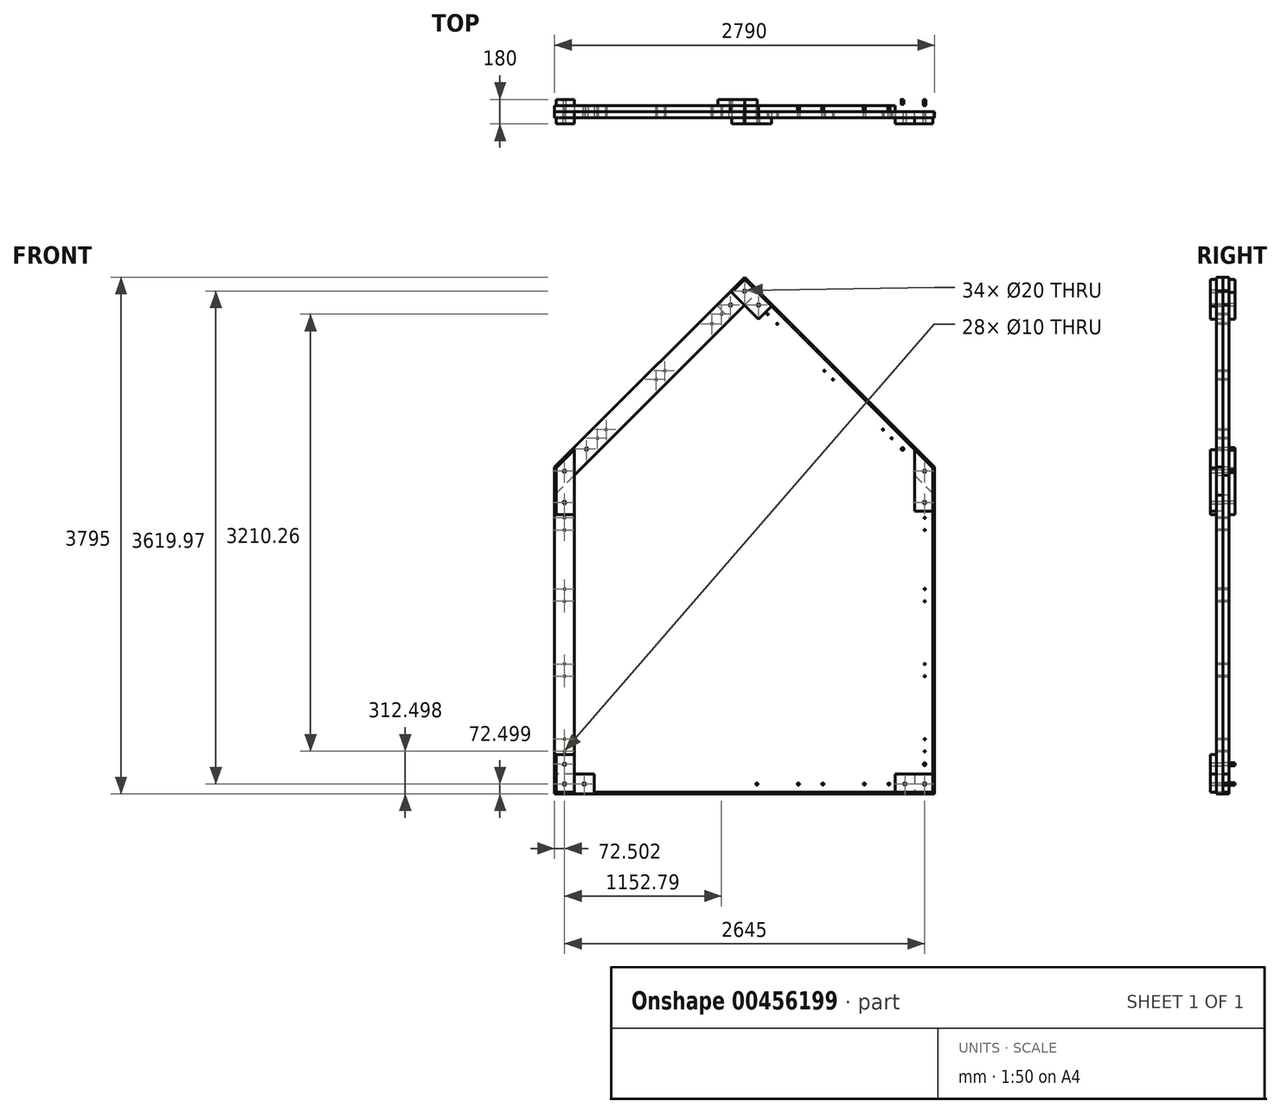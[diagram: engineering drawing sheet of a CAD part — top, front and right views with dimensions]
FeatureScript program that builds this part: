
annotation { "Feature Type Name" : "Feature", "Feature Type Description" : "" }
export const myFeature = defineFeature(function(context is Context, id is Id, definition is map)
    precondition{}
    {
        {
            var Q0;
            Q0=qCreatedBy(makeId("Front.planeOp"),FACE);
            var sketch = newSketch(context, id + "F0", { "sketchPlane" : qUnion([Q0])});
            skLineSegment(sketch, "E0.bottom", {"start": v(-2120.6, 125.67) * mm, "end": v(-4620.6, 125.67) * mm});
            skLineSegment(sketch, "E0.top", {"start": v(-2120.6, -2069.27) * mm, "end": v(-4620.6, -2069.27) * mm});
            skLineSegment(sketch, "E0.left", {"start": v(-2120.6, 125.67) * mm, "end": v(-2120.6, -2069.27) * mm});
            skLineSegment(sketch, "E0.right", {"start": v(-4620.6, 125.67) * mm, "end": v(-4620.6, -2069.27) * mm});
            skLineSegment(sketch, "E1", {"start": v(-4620.6, 125.67) * mm, "end": v(-3370.6, 1375.67) * mm});
            skPoint(sketch, "E1.endSnap0", {"position": v(-3370.6, 125.67) * mm});
            skLineSegment(sketch, "E2", {"start": v(-3370.6, 1375.67) * mm, "end": v(-2120.6, 125.67) * mm});
            skLineSegment(sketch, "E3.0", {"start": v(-3370.6, 1580.73) * mm, "end": v(-1975.6, 185.73) * mm});
            skLineSegment(sketch, "E3.1", {"start": v(-4765.6, 185.73) * mm, "end": v(-3370.6, 1580.73) * mm});
            skLineSegment(sketch, "E3.2", {"start": v(-1975.6, 185.73) * mm, "end": v(-1975.6, -2214.27) * mm});
            skLineSegment(sketch, "E3.3", {"start": v(-1975.6, -2214.27) * mm, "end": v(-4765.6, -2214.27) * mm});
            skLineSegment(sketch, "E3.4", {"start": v(-4765.6, 185.73) * mm, "end": v(-4765.6, -2214.27) * mm});
            skLineSegment(sketch, "E4", {"start": v(-4620.6, -2069.27) * mm, "end": v(-4765.6, -2069.27) * mm});
            skLineSegment(sketch, "E5", {"start": v(-4620.6, -2069.27) * mm, "end": v(-4620.6, -2214.27) * mm});
            skLineSegment(sketch, "E6", {"start": v(-2120.6, -2069.27) * mm, "end": v(-1975.6, -2069.27) * mm});
            skLineSegment(sketch, "E7", {"start": v(-2120.6, -2069.27) * mm, "end": v(-2120.6, -2214.27) * mm});
            skLineSegment(sketch, "E8", {"start": v(-3370.6, 1375.67) * mm, "end": v(-3268.07, 1478.2) * mm});
            skLineSegment(sketch, "E9", {"start": v(-3370.6, 1375.67) * mm, "end": v(-3473.13, 1478.2) * mm});
            skLineSegment(sketch, "E10", {"start": v(-4620.6, 125.67) * mm, "end": v(-4620.6, 330.73) * mm});
            skLineSegment(sketch, "E11", {"start": v(-4620.6, 125.67) * mm, "end": v(-4765.6, -19.33) * mm});
            skLineSegment(sketch, "E12", {"start": v(-2120.6, 125.67) * mm, "end": v(-1975.6, -19.33) * mm});
            skLineSegment(sketch, "E13", {"start": v(-2120.6, 125.67) * mm, "end": v(-2120.6, 330.73) * mm});
            skLineSegment(sketch, "E14", {"start": v(-4620.6, 125.67) * mm, "end": v(-4765.6, 185.73) * mm, "construction": true});
            skLineSegment(sketch, "E15", {"start": v(-4765.6, -1924.27) * mm, "end": v(-4620.6, -1924.27) * mm});
            skPoint(sketch, "E16", {"position": v(-4693.1, 155.7) * mm});
            skLineSegment(sketch, "E17", {"start": v(-4765.6, -134.3) * mm, "end": v(-4620.6, -134.3) * mm});
            skLineSegment(sketch, "E18", {"start": v(-4539.3, 412.02) * mm, "end": v(-4436.77, 309.5) * mm});
            skPoint(sketch, "E19", {"position": v(-4693.1, -74.3) * mm});
            skLineSegment(sketch, "E20", {"start": v(-3575.66, 1375.67) * mm, "end": v(-3473.13, 1273.14) * mm});
            skLineSegment(sketch, "E21", {"start": v(-4475.6, -2069.27) * mm, "end": v(-4475.6, -2214.27) * mm});
            skLineSegment(sketch, "E22", {"start": v(-4488.04, 360.76) * mm, "end": v(-3524.4, 1324.4) * mm, "construction": true});
            skPoint(sketch, "E23", {"position": v(-4440.3, 408.49) * mm});
            skPoint(sketch, "E24", {"position": v(-3572.12, 1276.67) * mm});
            skPoint(sketch, "E25", {"position": v(-4006.22, 842.58) * mm});
            skLineSegment(sketch, "E26", {"start": v(-2265.6, -2069.27) * mm, "end": v(-2265.6, -2214.27) * mm});
            skLineSegment(sketch, "E27", {"start": v(-4475.6, -2141.77) * mm, "end": v(-2265.6, -2141.77) * mm, "construction": true});
            skPoint(sketch, "E28", {"position": v(-4340.6, -2141.77) * mm});
            skPoint(sketch, "E29", {"position": v(-2400.6, -2141.77) * mm});
            skPoint(sketch, "E30", {"position": v(-3370.6, -2141.77) * mm});
            skLineSegment(sketch, "E31", {"start": v(-4340.6, -2141.77) * mm, "end": v(-3370.6, -2141.77) * mm, "construction": true});
            skLineSegment(sketch, "E32", {"start": v(-3370.6, -2141.77) * mm, "end": v(-2400.6, -2141.77) * mm, "construction": true});
            skPoint(sketch, "E33", {"position": v(-3855.6, -2141.77) * mm});
            skPoint(sketch, "E34", {"position": v(-2885.6, -2141.77) * mm});
            skLineSegment(sketch, "E35", {"start": v(-4693.1, 155.7) * mm, "end": v(-4488.04, 360.76) * mm, "construction": true});
            skPoint(sketch, "E36", {"position": v(-4693.1, -1996.77) * mm});
            skPoint(sketch, "E36.positionSnap0", {"position": v(-4693.1, -2069.27) * mm});
            skPoint(sketch, "E37", {"position": v(-4693.1, -2141.77) * mm});
            skPoint(sketch, "E38", {"position": v(-4548.1, -2141.77) * mm});
            skPoint(sketch, "E39.positionSnap0", {"position": v(-4693.1, -1924.27) * mm});
            skPoint(sketch, "E40", {"position": v(-4693.1, -174.3) * mm});
            skPoint(sketch, "E41.MirrorP", {"position": v(-4459.75, 389.04) * mm});
            skCircle(sketch, "E42", {"center": v(-4693.1, -1996.77) * mm, "radius": 10 * mm});
            skCircle(sketch, "E43", {"center": v(-4693.1, -2141.77) * mm, "radius": 10 * mm});
            skCircle(sketch, "E44", {"center": v(-4548.1, -2141.77) * mm, "radius": 10 * mm});
            skLineSegment(sketch, "E45", {"start": v(-3524.4, 1324.4) * mm, "end": v(-3421.86, 1426.93) * mm, "construction": true});
            skLineSegment(sketch, "E46", {"start": v(-3421.86, 1426.93) * mm, "end": v(-3319.33, 1529.46) * mm, "construction": true});
            skPoint(sketch, "E47", {"position": v(-3473.13, 1375.67) * mm});
            skPoint(sketch, "E48", {"position": v(-3370.6, 1478.2) * mm});
            skCircle(sketch, "E49", {"center": v(-3473.13, 1375.67) * mm, "radius": 10 * mm});
            skCircle(sketch, "E50", {"center": v(-3370.6, 1478.2) * mm, "radius": 10 * mm});
            skLineSegment(sketch, "E51", {"start": v(-3370.6, -2069.27) * mm, "end": v(-3370.6, -1584.54) * mm, "construction": true});
            skCircle(sketch, "E52.MirrorC", {"center": v(-2193.1, -2141.77) * mm, "radius": 10 * mm});
            skCircle(sketch, "E53.MirrorC", {"center": v(-2048.1, -2141.77) * mm, "radius": 10 * mm});
            skLineSegment(sketch, "E54.MirrorCS", {"start": v(-1975.6, -1924.27) * mm, "end": v(-2120.6, -1924.27) * mm});
            skCircle(sketch, "E55.MirrorC", {"center": v(-2048.1, -1996.77) * mm, "radius": 10 * mm});
            skCircle(sketch, "E56", {"center": v(-4693.1, 155.7) * mm, "radius": 10 * mm});
            skCircle(sketch, "E57", {"center": v(-4693.1, -74.3) * mm, "radius": 10 * mm});
            skCircle(sketch, "E58", {"center": v(-4530.46, 318.33) * mm, "radius": 10 * mm});
            skCircle(sketch, "E59.MirrorC", {"center": v(-2048.1, -74.3) * mm, "radius": 10 * mm});
            skCircle(sketch, "E60.MirrorC", {"center": v(-2048.1, 155.7) * mm, "radius": 10 * mm});
            skCircle(sketch, "E61.MirrorC", {"center": v(-2210.73, 318.33) * mm, "radius": 10 * mm});
            skCircle(sketch, "E62.MirrorC", {"center": v(-3268.07, 1375.67) * mm, "radius": 10 * mm});
            skLineSegment(sketch, "E63", {"start": v(-4620.6, -2024.27) * mm, "end": v(-2120.6, -2024.27) * mm});
            skLineSegment(sketch, "E64.0", {"start": v(-3370.6, 1340.31) * mm, "end": v(-2138.28, 107.99) * mm});
            skLineSegment(sketch, "E64.1", {"start": v(-4602.92, 107.99) * mm, "end": v(-3370.6, 1340.31) * mm});
            skLineSegment(sketch, "E65", {"start": v(-4595.6, -2024.27) * mm, "end": v(-4595.6, 115.31) * mm});
            skLineSegment(sketch, "E66", {"start": v(-4595.6, 115.31) * mm, "end": v(-4620.6, 125.67) * mm});
            skLineSegment(sketch, "E67.MirrorCS", {"start": v(-2145.6, -2024.27) * mm, "end": v(-2145.6, 115.31) * mm});
            skLineSegment(sketch, "E68", {"start": v(-3370.6, 1375.67) * mm, "end": v(-3370.6, 1340.31) * mm});
            skLineSegment(sketch, "E69", {"start": v(-2145.6, 115.31) * mm, "end": v(-2120.6, 125.67) * mm});
            skSolve(sketch);
        }
        {
            var Q0;
            {var subQ1=sQuery(id+"F0.wireOp",EDGE,"E4");Q0=makeQuery(id+"F0.imprint","IMPRINT",FACE,{"disambiguationData":[TD([[makeQuery(id+"F0.imprint","IMPRINT",EDGE,{"derivedFrom":subQ1}),1.0]])]});}
            var Q1;
            {var subQ0=sQuery(id+"F0.wireOp",EDGE,"E15");Q1=makeQuery(id+"F0.imprint","IMPRINT",FACE,{"disambiguationData":[TD([[makeQuery(id+"F0.imprint","IMPRINT",EDGE,{"derivedFrom":subQ0}),1.0]])]});}
            var Q2;
            {var subQ1=sQuery(id+"F0.wireOp",EDGE,"E4");Q2=makeQuery(id+"F0.imprint","IMPRINT",FACE,{"disambiguationData":[TD([[makeQuery(id+"F0.imprint","IMPRINT",EDGE,{"derivedFrom":subQ1}),-1.0]])]});}
            var Q3;
            {var subQ0=sQuery(id+"F0.wireOp",EDGE,"E11");Q3=makeQuery(id+"F0.imprint","IMPRINT",FACE,{"disambiguationData":[TD([[makeQuery(id+"F0.imprint","IMPRINT",EDGE,{"derivedFrom":subQ0}),1.0]])]});}
            extrude(context, id + "F1", {"entities" : qUnion([Q0, Q1, Q2, Q3]), "depth" : -45 * mm, "offsetDistance" : 25 * mm});
        }
        {
            var Q0;
            {var subQ1=sQuery(id+"F0.wireOp",EDGE,"E9");Q0=makeQuery(id+"F0.imprint","IMPRINT",FACE,{"disambiguationData":[TD([[makeQuery(id+"F0.imprint","IMPRINT",EDGE,{"derivedFrom":subQ1}),1.0]])]});}
            var Q1;
            {var subQ0=sQuery(id+"F0.wireOp",EDGE,"E18");Q1=makeQuery(id+"F0.imprint","IMPRINT",FACE,{"disambiguationData":[TD([[makeQuery(id+"F0.imprint","IMPRINT",EDGE,{"derivedFrom":subQ0}),1.0]])]});}
            var Q2;
            {var subQ0=sQuery(id+"F0.wireOp",EDGE,"E10");Q2=makeQuery(id+"F0.imprint","IMPRINT",FACE,{"disambiguationData":[TD([[makeQuery(id+"F0.imprint","IMPRINT",EDGE,{"derivedFrom":subQ0}),-1.0]])]});}
            var Q3;
            {var subQ4=sQuery(id+"F0.wireOp",EDGE,"E10");Q3=makeQuery(id+"F0.imprint","IMPRINT",FACE,{"disambiguationData":[TD([[makeQuery(id+"F0.imprint","IMPRINT",EDGE,{"derivedFrom":subQ4}),1.0]])]});}
            extrude(context, id + "F2", {"entities" : qUnion([Q0, Q1, Q2, Q3]), "depth" : -45 * mm, "offsetDistance" : 25 * mm});
        }
        {
            var Q0;
            {var subQ0=sQuery(id+"F0.wireOp",EDGE,"E8");Q0=makeQuery(id+"F0.imprint","IMPRINT",FACE,{"disambiguationData":[TD([[makeQuery(id+"F0.imprint","IMPRINT",EDGE,{"derivedFrom":subQ0}),1.0]])]});}
            var Q1;
            Q1=makeQuery(id+"F0.imprint","IMPRINT",FACE,{"disambiguationData":[TD([[makeQuery(id+"F0.imprint","IMPRINT",EDGE,{"derivedFrom":sQuery(id+"F0.wireOp",EDGE,"E2")}),1.0]])]});
            extrude(context, id + "F3", {"entities" : qUnion([Q0, Q1]), "depth" : -45 * mm, "offsetDistance" : 25 * mm});
        }
        {
            var Q0;
            {var subQ1=sQuery(id+"F0.wireOp",EDGE,"E12");Q0=makeQuery(id+"F0.imprint","IMPRINT",FACE,{"disambiguationData":[TD([[makeQuery(id+"F0.imprint","IMPRINT",EDGE,{"derivedFrom":subQ1}),1.0]])]});}
            var Q1;
            {var subQ1=sQuery(id+"F0.wireOp",EDGE,"E12");Q1=makeQuery(id+"F0.imprint","IMPRINT",FACE,{"disambiguationData":[TD([[makeQuery(id+"F0.imprint","IMPRINT",EDGE,{"derivedFrom":subQ1}),-1.0]])]});}
            var Q2;
            {var subQ0=sQuery(id+"F0.wireOp",EDGE,"E6");Q2=makeQuery(id+"F0.imprint","IMPRINT",FACE,{"disambiguationData":[TD([[makeQuery(id+"F0.imprint","IMPRINT",EDGE,{"derivedFrom":subQ0}),1.0]])]});}
            extrude(context, id + "F4", {"entities" : qUnion([Q0, Q1, Q2]), "depth" : -45 * mm, "offsetDistance" : 25 * mm});
        }
        {
            var Q0;
            {var subQ0=sQuery(id+"F0.wireOp",EDGE,"E21");Q0=makeQuery(id+"F0.imprint","IMPRINT",FACE,{"disambiguationData":[TD([[makeQuery(id+"F0.imprint","IMPRINT",EDGE,{"derivedFrom":subQ0}),1.0]])]});}
            var Q1;
            {var subQ1=sQuery(id+"F0.wireOp",EDGE,"E5");Q1=makeQuery(id+"F0.imprint","IMPRINT",FACE,{"disambiguationData":[TD([[makeQuery(id+"F0.imprint","IMPRINT",EDGE,{"derivedFrom":subQ1}),1.0]])]});}
            var Q2;
            {var subQ1=sQuery(id+"F0.wireOp",EDGE,"E7");Q2=makeQuery(id+"F0.imprint","IMPRINT",FACE,{"disambiguationData":[TD([[makeQuery(id+"F0.imprint","IMPRINT",EDGE,{"derivedFrom":subQ1}),-1.0]])]});}
            var Q3;
            {var subQ1=sQuery(id+"F0.wireOp",EDGE,"E6");Q3=makeQuery(id+"F0.imprint","IMPRINT",FACE,{"disambiguationData":[TD([[makeQuery(id+"F0.imprint","IMPRINT",EDGE,{"derivedFrom":subQ1}),-1.0]])]});}
            extrude(context, id + "F5", {"entities" : qUnion([Q0, Q1, Q2, Q3]), "depth" : -45 * mm, "offsetDistance" : 25 * mm});
        }
        {
            var Q0;
            {var subQ1=sQuery(id+"F0.wireOp",EDGE,"E4");Q0=makeQuery(id+"F0.imprint","IMPRINT",FACE,{"disambiguationData":[TD([[makeQuery(id+"F0.imprint","IMPRINT",EDGE,{"derivedFrom":subQ1}),1.0]])]});}
            var Q1;
            {var subQ1=sQuery(id+"F0.wireOp",EDGE,"E5");Q1=makeQuery(id+"F0.imprint","IMPRINT",FACE,{"disambiguationData":[TD([[makeQuery(id+"F0.imprint","IMPRINT",EDGE,{"derivedFrom":subQ1}),1.0]])]});}
            var Q2;
            {var subQ0=sQuery(id+"F0.wireOp",EDGE,"E21");Q2=makeQuery(id+"F0.imprint","IMPRINT",FACE,{"disambiguationData":[TD([[makeQuery(id+"F0.imprint","IMPRINT",EDGE,{"derivedFrom":subQ0}),1.0]])]});}
            var Q3;
            {var subQ1=sQuery(id+"F0.wireOp",EDGE,"E7");Q3=makeQuery(id+"F0.imprint","IMPRINT",FACE,{"disambiguationData":[TD([[makeQuery(id+"F0.imprint","IMPRINT",EDGE,{"derivedFrom":subQ1}),-1.0]])]});}
            extrude(context, id + "F6", {"entities" : qUnion([Q0, Q1, Q2, Q3]), "depth" : 45 * mm, "offsetDistance" : 25 * mm});
        }
        {
            var Q0;
            {var subQ1=sQuery(id+"F0.wireOp",EDGE,"E4");Q0=makeQuery(id+"F0.imprint","IMPRINT",FACE,{"disambiguationData":[TD([[makeQuery(id+"F0.imprint","IMPRINT",EDGE,{"derivedFrom":subQ1}),-1.0]])]});}
            var Q1;
            {var subQ0=sQuery(id+"F0.wireOp",EDGE,"E15");Q1=makeQuery(id+"F0.imprint","IMPRINT",FACE,{"disambiguationData":[TD([[makeQuery(id+"F0.imprint","IMPRINT",EDGE,{"derivedFrom":subQ0}),1.0]])]});}
            var Q2;
            {var subQ0=sQuery(id+"F0.wireOp",EDGE,"E11");Q2=makeQuery(id+"F0.imprint","IMPRINT",FACE,{"disambiguationData":[TD([[makeQuery(id+"F0.imprint","IMPRINT",EDGE,{"derivedFrom":subQ0}),1.0]])]});}
            var Q3;
            {var subQ4=sQuery(id+"F0.wireOp",EDGE,"E10");Q3=makeQuery(id+"F0.imprint","IMPRINT",FACE,{"disambiguationData":[TD([[makeQuery(id+"F0.imprint","IMPRINT",EDGE,{"derivedFrom":subQ4}),1.0]])]});}
            extrude(context, id + "F7", {"entities" : qUnion([Q0, Q1, Q2, Q3]), "depth" : 45 * mm, "offsetDistance" : 25 * mm});
        }
        {
            var Q0;
            {var subQ0=sQuery(id+"F0.wireOp",EDGE,"E10");Q0=makeQuery(id+"F0.imprint","IMPRINT",FACE,{"disambiguationData":[TD([[makeQuery(id+"F0.imprint","IMPRINT",EDGE,{"derivedFrom":subQ0}),-1.0]])]});}
            var Q1;
            {var subQ0=sQuery(id+"F0.wireOp",EDGE,"E18");Q1=makeQuery(id+"F0.imprint","IMPRINT",FACE,{"disambiguationData":[TD([[makeQuery(id+"F0.imprint","IMPRINT",EDGE,{"derivedFrom":subQ0}),1.0]])]});}
            var Q2;
            {var subQ1=sQuery(id+"F0.wireOp",EDGE,"E9");Q2=makeQuery(id+"F0.imprint","IMPRINT",FACE,{"disambiguationData":[TD([[makeQuery(id+"F0.imprint","IMPRINT",EDGE,{"derivedFrom":subQ1}),1.0]])]});}
            var Q3;
            {var subQ0=sQuery(id+"F0.wireOp",EDGE,"E8");Q3=makeQuery(id+"F0.imprint","IMPRINT",FACE,{"disambiguationData":[TD([[makeQuery(id+"F0.imprint","IMPRINT",EDGE,{"derivedFrom":subQ0}),1.0]])]});}
            extrude(context, id + "F8", {"entities" : qUnion([Q0, Q1, Q2, Q3]), "depth" : 45 * mm, "offsetDistance" : 25 * mm});
        }
        {
            var Q0;
            Q0=makeQuery(id+"F0.imprint","IMPRINT",FACE,{"disambiguationData":[TD([[makeQuery(id+"F0.imprint","IMPRINT",EDGE,{"derivedFrom":sQuery(id+"F0.wireOp",EDGE,"E2")}),1.0]])]});
            var Q1;
            {var subQ1=sQuery(id+"F0.wireOp",EDGE,"E12");Q1=makeQuery(id+"F0.imprint","IMPRINT",FACE,{"disambiguationData":[TD([[makeQuery(id+"F0.imprint","IMPRINT",EDGE,{"derivedFrom":subQ1}),1.0]])]});}
            extrude(context, id + "F9", {"entities" : qUnion([Q0, Q1]), "depth" : 45 * mm, "offsetDistance" : 25 * mm});
        }
        {
            var Q0;
            {var subQ1=sQuery(id+"F0.wireOp",EDGE,"E12");Q0=makeQuery(id+"F0.imprint","IMPRINT",FACE,{"disambiguationData":[TD([[makeQuery(id+"F0.imprint","IMPRINT",EDGE,{"derivedFrom":subQ1}),-1.0]])]});}
            var Q1;
            {var subQ0=sQuery(id+"F0.wireOp",EDGE,"E6");Q1=makeQuery(id+"F0.imprint","IMPRINT",FACE,{"disambiguationData":[TD([[makeQuery(id+"F0.imprint","IMPRINT",EDGE,{"derivedFrom":subQ0}),1.0]])]});}
            var Q2;
            {var subQ1=sQuery(id+"F0.wireOp",EDGE,"E6");Q2=makeQuery(id+"F0.imprint","IMPRINT",FACE,{"disambiguationData":[TD([[makeQuery(id+"F0.imprint","IMPRINT",EDGE,{"derivedFrom":subQ1}),-1.0]])]});}
            extrude(context, id + "F10", {"entities" : qUnion([Q0, Q1, Q2]), "depth" : 45 * mm, "offsetDistance" : 25 * mm});
        }
        {
            var Q0;
            Q0=makeQuery(id+"F7.opExtrude","CAP_FACE",FACE,{"disambiguationData":[OSD([sQuery(id+"F0.wireOp",EDGE,"E0.right"),sQuery(id+"F0.wireOp",EDGE,"E3.1"),sQuery(id+"F0.wireOp",EDGE,"E3.4"),sQuery(id+"F0.wireOp",EDGE,"E4"),sQuery(id+"F0.wireOp",EDGE,"E10"),sQuery(id+"F0.wireOp",EDGE,"E42"),sQuery(id+"F0.wireOp",EDGE,"E56"),sQuery(id+"F0.wireOp",EDGE,"E57")])],"isStart":false});
            var sketch = newSketch(context, id + "F11", { "sketchPlane" : qUnion([Q0])});
            skLineSegment(sketch, "E70.bottom", {"start": v(-4765.6, -2069.27) * mm, "end": v(-1975.6, -2069.27) * mm});
            skLineSegment(sketch, "E70.top", {"start": v(-4765.6, -2214.27) * mm, "end": v(-1975.6, -2214.27) * mm});
            skLineSegment(sketch, "E70.left", {"start": v(-4765.6, -2069.27) * mm, "end": v(-4765.6, -2214.27) * mm});
            skLineSegment(sketch, "E70.right", {"start": v(-1975.6, -2069.27) * mm, "end": v(-1975.6, -2214.27) * mm});
            skLineSegment(sketch, "E71", {"start": v(-4765.6, -2069.27) * mm, "end": v(-4765.6, 185.73) * mm});
            skLineSegment(sketch, "E72", {"start": v(-1975.6, -2069.27) * mm, "end": v(-1975.6, 185.73) * mm});
            skLineSegment(sketch, "E73", {"start": v(-4765.6, 185.73) * mm, "end": v(-3370.6, 1580.73) * mm});
            skLineSegment(sketch, "E74", {"start": v(-3370.6, 1580.73) * mm, "end": v(-1975.6, 185.73) * mm});
            skLineSegment(sketch, "E75.0", {"start": v(-3370.6, 1375.67) * mm, "end": v(-2120.6, 125.67) * mm});
            skLineSegment(sketch, "E75.1", {"start": v(-4620.6, 125.67) * mm, "end": v(-3370.6, 1375.67) * mm});
            skLineSegment(sketch, "E75.2", {"start": v(-2120.6, -2069.27) * mm, "end": v(-2120.6, 125.67) * mm});
            skLineSegment(sketch, "E75.3", {"start": v(-4620.6, -2069.27) * mm, "end": v(-2120.6, -2069.27) * mm});
            skLineSegment(sketch, "E75.4", {"start": v(-4620.6, -2069.27) * mm, "end": v(-4620.6, 125.67) * mm});
            skLineSegment(sketch, "E76", {"start": v(-4620.6, 125.67) * mm, "end": v(-4765.6, -19.33) * mm});
            skLineSegment(sketch, "E77", {"start": v(-4765.6, -164.33) * mm, "end": v(-4620.6, -164.33) * mm});
            skLineSegment(sketch, "E78", {"start": v(-4518.07, 433.26) * mm, "end": v(-4415.54, 330.73) * mm});
            skCircle(sketch, "E79", {"center": v(-4693.1, -74.3) * mm, "radius": 10 * mm});
            skCircle(sketch, "E80", {"center": v(-4693.1, 155.7) * mm, "radius": 10 * mm});
            skCircle(sketch, "E81", {"center": v(-4693.1, -1996.77) * mm, "radius": 10 * mm});
            skLineSegment(sketch, "E82", {"start": v(-4693.1, 155.7) * mm, "end": v(-3319.33, 1529.46) * mm, "construction": true});
            skPoint(sketch, "E83", {"position": v(-3370.6, 1478.2) * mm});
            skPoint(sketch, "E84", {"position": v(-3473.13, 1375.67) * mm});
            skPoint(sketch, "E85", {"position": v(-4530.46, 318.33) * mm});
            skCircle(sketch, "E86", {"center": v(-4530.46, 318.33) * mm, "radius": 10 * mm});
            skCircle(sketch, "E87", {"center": v(-4693.1, -2141.77) * mm, "radius": 10 * mm});
            skCircle(sketch, "E88", {"center": v(-4548.1, -2141.77) * mm, "radius": 10 * mm});
            skLineSegment(sketch, "E89", {"start": v(-4475.6, -2069.27) * mm, "end": v(-4475.6, -2214.27) * mm});
            skLineSegment(sketch, "E90", {"start": v(-4765.6, -1924.27) * mm, "end": v(-4620.6, -1924.27) * mm});
            skLineSegment(sketch, "E91", {"start": v(-4620.6, -2069.27) * mm, "end": v(-4620.6, -2214.27) * mm});
            skLineSegment(sketch, "E92", {"start": v(-3370.6, 1375.67) * mm, "end": v(-3473.13, 1478.2) * mm});
            skLineSegment(sketch, "E93", {"start": v(-3268.07, 1273.14) * mm, "end": v(-3165.54, 1375.67) * mm});
            skLineSegment(sketch, "E94", {"start": v(-3370.6, 1478.2) * mm, "end": v(-3268.07, 1375.67) * mm, "construction": true});
            skCircle(sketch, "E95", {"center": v(-3370.6, 1478.2) * mm, "radius": 10 * mm});
            skCircle(sketch, "E96", {"center": v(-3268.07, 1375.67) * mm, "radius": 10 * mm});
            skLineSegment(sketch, "E97", {"start": v(-2120.6, 125.67) * mm, "end": v(-2120.6, 330.73) * mm});
            skLineSegment(sketch, "E98", {"start": v(-2120.6, -139.1) * mm, "end": v(-1975.6, -139.1) * mm});
            skLineSegment(sketch, "E99", {"start": v(-2048.1, -139.1) * mm, "end": v(-2048.1, 258.23) * mm, "construction": true});
            skLineSegment(sketch, "E100", {"start": v(-3268.07, 1375.67) * mm, "end": v(-1975.6, 83.2) * mm, "construction": true});
            skCircle(sketch, "E101", {"center": v(-2048.1, 155.7) * mm, "radius": 10 * mm});
            skCircle(sketch, "E102", {"center": v(-2048.1, -74.3) * mm, "radius": 10 * mm});
            skLineSegment(sketch, "E103", {"start": v(-2265.6, -2069.27) * mm, "end": v(-2265.6, -2214.27) * mm});
            skLineSegment(sketch, "E104", {"start": v(-2265.6, -2141.77) * mm, "end": v(-1975.6, -2141.77) * mm, "construction": true});
            skCircle(sketch, "E105", {"center": v(-2048.1, -2141.77) * mm, "radius": 10 * mm});
            skCircle(sketch, "E106", {"center": v(-2193.1, -2141.77) * mm, "radius": 10 * mm});
            skLineSegment(sketch, "E107.0", {"start": v(-4753.6, -2069.27) * mm, "end": v(-4753.6, -2202.27) * mm});
            skLineSegment(sketch, "E107.1", {"start": v(-4753.6, -2202.27) * mm, "end": v(-1987.6, -2202.27) * mm});
            skLineSegment(sketch, "E107.2", {"start": v(-4753.6, 180.76) * mm, "end": v(-3370.6, 1563.76) * mm});
            skLineSegment(sketch, "E107.3", {"start": v(-3370.6, 1563.76) * mm, "end": v(-1987.6, 180.76) * mm});
            skLineSegment(sketch, "E107.4", {"start": v(-1987.6, -2069.27) * mm, "end": v(-1987.6, 180.76) * mm});
            skLineSegment(sketch, "E107.5", {"start": v(-4753.6, -2069.27) * mm, "end": v(-4753.6, 180.76) * mm});
            skLineSegment(sketch, "E107.6", {"start": v(-1987.6, -2069.27) * mm, "end": v(-1987.6, -2202.27) * mm});
            skLineSegment(sketch, "E108", {"start": v(-4475.6, -2141.77) * mm, "end": v(-2265.6, -2141.77) * mm, "construction": true});
            skLineSegment(sketch, "E109", {"start": v(-4693.1, -164.33) * mm, "end": v(-4693.1, -1924.27) * mm, "construction": true});
            skCircle(sketch, "E110", {"center": v(-4430.6, -2141.77) * mm, "radius": 8 * mm});
            skCircle(sketch, "E111", {"center": v(-4250.6, -2141.77) * mm, "radius": 8 * mm});
            skCircle(sketch, "E112", {"center": v(-3945.6, -2141.77) * mm, "radius": 8 * mm});
            skCircle(sketch, "E113", {"center": v(-4693.1, -1901.77) * mm, "radius": 5 * mm});
            skCircle(sketch, "E114", {"center": v(-4693.1, -1811.77) * mm, "radius": 5 * mm});
            skCircle(sketch, "E115", {"center": v(-4693.1, -1350.77) * mm, "radius": 5 * mm});
            skCircle(sketch, "E116", {"center": v(-4693.1, -1260.77) * mm, "radius": 5 * mm});
            skCircle(sketch, "E117", {"center": v(-4693.1, -799.77) * mm, "radius": 5 * mm});
            skCircle(sketch, "E118", {"center": v(-4693.1, -709.77) * mm, "radius": 5 * mm});
            skCircle(sketch, "E119", {"center": v(-4693.1, -186.83) * mm, "radius": 5 * mm});
            skCircle(sketch, "E120", {"center": v(-4693.1, -276.83) * mm, "radius": 5 * mm});
            skCircle(sketch, "E121", {"center": v(-4450.9, 397.9) * mm, "radius": 5 * mm});
            skCircle(sketch, "E122", {"center": v(-4387.25, 461.54) * mm, "radius": 5 * mm});
            skCircle(sketch, "E123", {"center": v(-3540.3, 1308.5) * mm, "radius": 5 * mm});
            skCircle(sketch, "E124", {"center": v(-3611.01, 1237.78) * mm, "radius": 5 * mm});
            skCircle(sketch, "E125", {"center": v(-4019.56, 829.24) * mm, "radius": 5 * mm});
            skCircle(sketch, "E126", {"center": v(-3955.92, 892.88) * mm, "radius": 5 * mm});
            skCircle(sketch, "E127", {"center": v(-3765.6, -2141.77) * mm, "radius": 8 * mm});
            skCircle(sketch, "E128", {"center": v(-3460.6, -2141.77) * mm, "radius": 8 * mm});
            skLineSegment(sketch, "E129", {"start": v(-3370.6, -2202.27) * mm, "end": v(-3370.6, -2069.27) * mm, "construction": true});
            skCircle(sketch, "E130.MirrorC", {"center": v(-3200.9, 1308.5) * mm, "radius": 5 * mm});
            skCircle(sketch, "E131.MirrorC", {"center": v(-3130.18, 1237.78) * mm, "radius": 5 * mm});
            skCircle(sketch, "E132.MirrorC", {"center": v(-2721.64, 829.24) * mm, "radius": 5 * mm});
            skCircle(sketch, "E133.MirrorC", {"center": v(-2353.94, 461.54) * mm, "radius": 5 * mm});
            skCircle(sketch, "E134.MirrorC", {"center": v(-2290.3, 397.9) * mm, "radius": 5 * mm});
            skCircle(sketch, "E135.MirrorC", {"center": v(-2048.1, -186.83) * mm, "radius": 5 * mm});
            skCircle(sketch, "E136.MirrorC", {"center": v(-2048.1, -276.83) * mm, "radius": 5 * mm});
            skCircle(sketch, "E137.MirrorC", {"center": v(-2048.1, -709.77) * mm, "radius": 5 * mm});
            skCircle(sketch, "E138.MirrorC", {"center": v(-2048.1, -799.77) * mm, "radius": 5 * mm});
            skCircle(sketch, "E139.MirrorC", {"center": v(-2048.1, -1260.77) * mm, "radius": 5 * mm});
            skCircle(sketch, "E140.MirrorC", {"center": v(-2048.1, -1350.77) * mm, "radius": 5 * mm});
            skCircle(sketch, "E141.MirrorC", {"center": v(-2048.1, -1811.77) * mm, "radius": 5 * mm});
            skCircle(sketch, "E142.MirrorC", {"center": v(-2048.1, -1901.77) * mm, "radius": 5 * mm});
            skCircle(sketch, "E143.MirrorC", {"center": v(-2310.6, -2141.77) * mm, "radius": 8 * mm});
            skCircle(sketch, "E144.MirrorC", {"center": v(-2490.6, -2141.77) * mm, "radius": 8 * mm});
            skCircle(sketch, "E145.MirrorC", {"center": v(-2795.6, -2141.77) * mm, "radius": 8 * mm});
            skCircle(sketch, "E146.MirrorC", {"center": v(-2975.6, -2141.77) * mm, "radius": 8 * mm});
            skCircle(sketch, "E147.MirrorC", {"center": v(-3280.6, -2141.77) * mm, "radius": 8 * mm});
            skCircle(sketch, "E148.MirrorC", {"center": v(-2785.28, 892.88) * mm, "radius": 5 * mm});
            skSolve(sketch);
        }
        {
            var Q0;
            Q0=makeQuery(id+"F11.imprint","IMPRINT",FACE,{"disambiguationData":[TD([[makeQuery(id+"F11.imprint","IMPRINT",EDGE,{"derivedFrom":sQuery(id+"F11.wireOp",EDGE,"E79")}),-1.0]])]});
            var Q1;
            Q1=makeQuery(id+"F11.imprint","IMPRINT",FACE,{"disambiguationData":[TD([[makeQuery(id+"F11.imprint","IMPRINT",EDGE,{"derivedFrom":sQuery(id+"F11.wireOp",EDGE,"E80")}),-1.0]])]});
            var Q2;
            Q2=makeQuery(id+"F11.imprint","IMPRINT",FACE,{"disambiguationData":[TD([[makeQuery(id+"F11.imprint","IMPRINT",EDGE,{"derivedFrom":sQuery(id+"F11.wireOp",EDGE,"E81")}),-1.0]])]});
            var Q3;
            Q3=makeQuery(id+"F11.imprint","IMPRINT",FACE,{"disambiguationData":[TD([[makeQuery(id+"F11.imprint","IMPRINT",EDGE,{"derivedFrom":sQuery(id+"F11.wireOp",EDGE,"E87")}),-1.0]])]});
            var Q4;
            Q4=makeQuery(id+"F11.imprint","IMPRINT",FACE,{"disambiguationData":[TD([[makeQuery(id+"F11.imprint","IMPRINT",EDGE,{"derivedFrom":sQuery(id+"F11.wireOp",EDGE,"E105")}),-1.0]])]});
            var Q5;
            Q5=makeQuery(id+"F11.imprint","IMPRINT",FACE,{"disambiguationData":[TD([[makeQuery(id+"F11.imprint","IMPRINT",EDGE,{"derivedFrom":sQuery(id+"F11.wireOp",EDGE,"E101")}),-1.0]])]});
            var Q6;
            Q6=makeQuery(id+"F11.imprint","IMPRINT",FACE,{"disambiguationData":[TD([[makeQuery(id+"F11.imprint","IMPRINT",EDGE,{"derivedFrom":sQuery(id+"F11.wireOp",EDGE,"E95")}),-1.0]])]});
            extrude(context, id + "F12", {"entities" : qUnion([Q0, Q1, Q2, Q3, Q4, Q5, Q6]), "depth" : 45 * mm, "offsetDistance" : 25 * mm});
        }
        {
            var Q0;
            Q0=makeQuery(id+"F4.opExtrude","CAP_FACE",FACE,{"disambiguationData":[OSD([sQuery(id+"F0.wireOp",EDGE,"E0.left"),sQuery(id+"F0.wireOp",EDGE,"E3.0"),sQuery(id+"F0.wireOp",EDGE,"E3.2"),sQuery(id+"F0.wireOp",EDGE,"E6"),sQuery(id+"F0.wireOp",EDGE,"E13"),sQuery(id+"F0.wireOp",EDGE,"E55.MirrorC"),sQuery(id+"F0.wireOp",EDGE,"E59.MirrorC"),sQuery(id+"F0.wireOp",EDGE,"E60.MirrorC")])],"isStart":false});
            var sketch = newSketch(context, id + "F13", { "sketchPlane" : qUnion([Q0])});
            skLineSegment(sketch, "E149.bottom", {"start": v(1975.6, -2069.27) * mm, "end": v(4765.6, -2069.27) * mm});
            skLineSegment(sketch, "E149.top", {"start": v(1975.6, -2214.27) * mm, "end": v(4765.6, -2214.27) * mm});
            skLineSegment(sketch, "E149.left", {"start": v(1975.6, -2069.27) * mm, "end": v(1975.6, -2214.27) * mm});
            skLineSegment(sketch, "E149.right", {"start": v(4765.6, -2069.27) * mm, "end": v(4765.6, -2214.27) * mm});
            skLineSegment(sketch, "E150", {"start": v(1975.6, -2069.27) * mm, "end": v(1975.6, 185.73) * mm});
            skLineSegment(sketch, "E151", {"start": v(4765.6, -2069.27) * mm, "end": v(4765.6, 185.73) * mm});
            skLineSegment(sketch, "E152", {"start": v(1975.6, 185.73) * mm, "end": v(3370.6, 1580.73) * mm});
            skLineSegment(sketch, "E153", {"start": v(3370.6, 1580.73) * mm, "end": v(4765.6, 185.73) * mm});
            skLineSegment(sketch, "E154.0", {"start": v(4620.6, -2069.27) * mm, "end": v(4620.6, 125.67) * mm});
            skLineSegment(sketch, "E154.1", {"start": v(3370.6, 1375.67) * mm, "end": v(4620.6, 125.67) * mm});
            skLineSegment(sketch, "E154.2", {"start": v(2120.6, -2069.27) * mm, "end": v(4620.6, -2069.27) * mm});
            skLineSegment(sketch, "E154.3", {"start": v(2120.6, -2069.27) * mm, "end": v(2120.6, 125.67) * mm});
            skLineSegment(sketch, "E154.4", {"start": v(2120.6, 125.67) * mm, "end": v(3370.6, 1375.67) * mm});
            skLineSegment(sketch, "E155.bottom", {"start": v(1975.6, -2214.27) * mm, "end": v(2120.6, -2214.27) * mm});
            skLineSegment(sketch, "E155.top", {"start": v(1975.6, -1924.27) * mm, "end": v(2120.6, -1924.27) * mm});
            skLineSegment(sketch, "E155.left", {"start": v(1975.6, -2214.27) * mm, "end": v(1975.6, -1924.27) * mm});
            skLineSegment(sketch, "E155.right", {"start": v(2120.6, -2214.27) * mm, "end": v(2120.6, -1924.27) * mm});
            skLineSegment(sketch, "E156.bottom", {"start": v(4765.6, -2214.27) * mm, "end": v(4475.6, -2214.27) * mm});
            skLineSegment(sketch, "E156.top", {"start": v(4765.6, -2069.27) * mm, "end": v(4475.6, -2069.27) * mm});
            skLineSegment(sketch, "E156.left", {"start": v(4765.6, -2214.27) * mm, "end": v(4765.6, -2069.27) * mm});
            skLineSegment(sketch, "E156.right", {"start": v(4475.6, -2214.27) * mm, "end": v(4475.6, -2069.27) * mm});
            skLineSegment(sketch, "E157", {"start": v(3370.6, 1375.67) * mm, "end": v(3268.07, 1478.2) * mm});
            skLineSegment(sketch, "E158", {"start": v(3268.07, 1478.2) * mm, "end": v(3370.6, 1580.73) * mm});
            skLineSegment(sketch, "E159", {"start": v(3575.66, 1375.67) * mm, "end": v(3473.13, 1273.14) * mm});
            skLineSegment(sketch, "E160", {"start": v(3319.33, 1529.46) * mm, "end": v(4765.6, 83.2) * mm, "construction": true});
            skLineSegment(sketch, "E161", {"start": v(4765.6, -2214.27) * mm, "end": v(4620.6, -2214.27) * mm});
            skLineSegment(sketch, "E162", {"start": v(4693.1, -2214.27) * mm, "end": v(4693.1, 258.23) * mm, "construction": true});
            skLineSegment(sketch, "E163", {"start": v(2120.6, 125.67) * mm, "end": v(1975.6, -19.33) * mm});
            skLineSegment(sketch, "E164", {"start": v(2223.13, 433.26) * mm, "end": v(2325.66, 330.73) * mm});
            skLineSegment(sketch, "E165", {"start": v(4620.6, -164.33) * mm, "end": v(4765.6, -164.33) * mm});
            skLineSegment(sketch, "E166", {"start": v(4620.6, 125.67) * mm, "end": v(4620.6, 330.73) * mm});
            skLineSegment(sketch, "E167.0", {"start": v(4753.6, -2069.27) * mm, "end": v(4753.6, 180.76) * mm});
            skLineSegment(sketch, "E167.1", {"start": v(3370.6, 1563.76) * mm, "end": v(4753.6, 180.76) * mm});
            skLineSegment(sketch, "E167.2", {"start": v(1987.6, -2202.27) * mm, "end": v(4765.6, -2202.27) * mm});
            skLineSegment(sketch, "E167.3", {"start": v(1987.6, -2069.27) * mm, "end": v(1987.6, -2202.27) * mm});
            skLineSegment(sketch, "E167.4", {"start": v(1987.6, -2069.27) * mm, "end": v(1987.6, 180.76) * mm});
            skLineSegment(sketch, "E167.5", {"start": v(1987.6, 180.76) * mm, "end": v(3370.6, 1563.76) * mm});
            skSolve(sketch);
        }
        {
            var Q0;
            {var subQ3=sQuery(id+"F13.wireOp",EDGE,"E159");var subQ5=sQuery(id+"F13.wireOp",EDGE,"E154.1");var subQ6=makeQuery(id+"F13.imprint","INTERSECT",VERTEX,{"derivedFrom":[subQ5,subQ3]});Q0=makeQuery(id+"F13.imprint","IMPRINT",FACE,{"disambiguationData":[TD([[makeQuery(id+"F13.imprint","IMPRINT",EDGE,{"disambiguationData":[TD([[subQ6,1.0]])],"derivedFrom":subQ3}),-1.0]])]});}
            var Q1;
            Q1=makeQuery(id+"F13.imprint","IMPRINT",FACE,{"disambiguationData":[TD([[makeQuery(id+"F13.imprint","IMPRINT",EDGE,{"derivedFrom":makeQuery(id+"F4.opExtrude","CAP_EDGE",EDGE,{"disambiguationData":[OSD([sQuery(id+"F0.wireOp",EDGE,"E60.MirrorC")])],"isStart":false})}),-1.0]])]});
            var Q2;
            {var subQ0=sQuery(id+"F13.wireOp",EDGE,"E154.4");var subQ3=sQuery(id+"F13.wireOp",EDGE,"E164");var subQ4=makeQuery(id+"F13.imprint","INTERSECT",VERTEX,{"derivedFrom":[subQ0,subQ3]});Q2=makeQuery(id+"F13.imprint","IMPRINT",FACE,{"disambiguationData":[TD([[makeQuery(id+"F13.imprint","IMPRINT",EDGE,{"disambiguationData":[TD([[subQ4,1.0]])],"derivedFrom":subQ3}),-1.0]])]});}
            var Q3;
            Q3=makeQuery(id+"F13.imprint","IMPRINT",FACE,{"disambiguationData":[TD([[makeQuery(id+"F13.imprint","IMPRINT",EDGE,{"derivedFrom":makeQuery(id+"F4.opExtrude","CAP_EDGE",EDGE,{"disambiguationData":[OSD([sQuery(id+"F0.wireOp",EDGE,"E55.MirrorC")])],"isStart":false})}),-1.0]])]});
            var Q4;
            {var subQ3=sQuery(id+"F13.wireOp",EDGE,"E167.3");Q4=makeQuery(id+"F13.imprint","IMPRINT",FACE,{"disambiguationData":[TD([[makeQuery(id+"F13.imprint","IMPRINT",EDGE,{"derivedFrom":subQ3}),1.0]])]});}
            var Q5;
            {var subQ1=sQuery(id+"F13.wireOp",EDGE,"E156.top");var subQ5=makeQuery(id+"F13.imprint","INTERSECT",VERTEX,{"derivedFrom":[sQuery(id+"F13.wireOp",EDGE,"E154.0"),subQ1]});Q5=makeQuery(id+"F13.imprint","IMPRINT",FACE,{"disambiguationData":[TD([[makeQuery(id+"F13.imprint","IMPRINT",EDGE,{"disambiguationData":[TD([[subQ5,1.0]])],"derivedFrom":subQ1}),1.0]])]});}
            var Q6;
            {var subQ3=sQuery(id+"F13.wireOp",EDGE,"E165");var subQ5=sQuery(id+"F13.wireOp",EDGE,"E154.0");var subQ6=makeQuery(id+"F13.imprint","INTERSECT",VERTEX,{"derivedFrom":[subQ5,subQ3]});Q6=makeQuery(id+"F13.imprint","IMPRINT",FACE,{"disambiguationData":[TD([[makeQuery(id+"F13.imprint","IMPRINT",EDGE,{"disambiguationData":[TD([[subQ6,-1.0]])],"derivedFrom":subQ3}),1.0]])]});}
            extrude(context, id + "F14", {"entities" : qUnion([Q0, Q1, Q2, Q3, Q4, Q5, Q6]), "depth" : 45 * mm, "offsetDistance" : 25 * mm});
        }
        {
            var Q0;
            Q0=makeQuery(id+"F0.imprint","IMPRINT",FACE,{"disambiguationData":[TD([[makeQuery(id+"F0.imprint","IMPRINT",EDGE,{"derivedFrom":sQuery(id+"F0.wireOp",EDGE,"E49")}),1.0]])]});
            var Q1;
            Q1=makeQuery(id+"F0.imprint","IMPRINT",FACE,{"disambiguationData":[TD([[makeQuery(id+"F0.imprint","IMPRINT",EDGE,{"derivedFrom":sQuery(id+"F0.wireOp",EDGE,"E50")}),-1.0]])]});
            var Q2;
            Q2=makeQuery(id+"F0.imprint","IMPRINT",FACE,{"disambiguationData":[TD([[makeQuery(id+"F0.imprint","IMPRINT",EDGE,{"derivedFrom":sQuery(id+"F0.wireOp",EDGE,"E62.MirrorC")}),-1.0]])]});
            var Q3;
            Q3=makeQuery(id+"F0.imprint","IMPRINT",FACE,{"disambiguationData":[TD([[makeQuery(id+"F0.imprint","IMPRINT",EDGE,{"derivedFrom":sQuery(id+"F0.wireOp",EDGE,"E58")}),1.0]])]});
            var Q4;
            Q4=makeQuery(id+"F0.imprint","IMPRINT",FACE,{"disambiguationData":[TD([[makeQuery(id+"F0.imprint","IMPRINT",EDGE,{"derivedFrom":sQuery(id+"F0.wireOp",EDGE,"E56")}),1.0]])]});
            var Q5;
            Q5=makeQuery(id+"F0.imprint","IMPRINT",FACE,{"disambiguationData":[TD([[makeQuery(id+"F0.imprint","IMPRINT",EDGE,{"derivedFrom":sQuery(id+"F0.wireOp",EDGE,"E57")}),1.0]])]});
            var Q6;
            Q6=makeQuery(id+"F0.imprint","IMPRINT",FACE,{"disambiguationData":[TD([[makeQuery(id+"F0.imprint","IMPRINT",EDGE,{"derivedFrom":sQuery(id+"F0.wireOp",EDGE,"E42")}),1.0]])]});
            var Q7;
            Q7=makeQuery(id+"F0.imprint","IMPRINT",FACE,{"disambiguationData":[TD([[makeQuery(id+"F0.imprint","IMPRINT",EDGE,{"derivedFrom":sQuery(id+"F0.wireOp",EDGE,"E43")}),1.0]])]});
            var Q8;
            Q8=makeQuery(id+"F0.imprint","IMPRINT",FACE,{"disambiguationData":[TD([[makeQuery(id+"F0.imprint","IMPRINT",EDGE,{"derivedFrom":sQuery(id+"F0.wireOp",EDGE,"E44")}),1.0]])]});
            var Q9;
            Q9=makeQuery(id+"F0.imprint","IMPRINT",FACE,{"disambiguationData":[TD([[makeQuery(id+"F0.imprint","IMPRINT",EDGE,{"derivedFrom":sQuery(id+"F0.wireOp",EDGE,"E52.MirrorC")}),-1.0]])]});
            var Q10;
            Q10=makeQuery(id+"F0.imprint","IMPRINT",FACE,{"disambiguationData":[TD([[makeQuery(id+"F0.imprint","IMPRINT",EDGE,{"derivedFrom":sQuery(id+"F0.wireOp",EDGE,"E53.MirrorC")}),-1.0]])]});
            var Q11;
            Q11=makeQuery(id+"F0.imprint","IMPRINT",FACE,{"disambiguationData":[TD([[makeQuery(id+"F0.imprint","IMPRINT",EDGE,{"derivedFrom":sQuery(id+"F0.wireOp",EDGE,"E55.MirrorC")}),-1.0]])]});
            var Q12;
            Q12=makeQuery(id+"F0.imprint","IMPRINT",FACE,{"disambiguationData":[TD([[makeQuery(id+"F0.imprint","IMPRINT",EDGE,{"derivedFrom":sQuery(id+"F0.wireOp",EDGE,"E59.MirrorC")}),-1.0]])]});
            var Q13;
            Q13=makeQuery(id+"F0.imprint","IMPRINT",FACE,{"disambiguationData":[TD([[makeQuery(id+"F0.imprint","IMPRINT",EDGE,{"derivedFrom":sQuery(id+"F0.wireOp",EDGE,"E60.MirrorC")}),-1.0]])]});
            var Q14;
            Q14=makeQuery(id+"F0.imprint","IMPRINT",FACE,{"disambiguationData":[TD([[makeQuery(id+"F0.imprint","IMPRINT",EDGE,{"derivedFrom":sQuery(id+"F0.wireOp",EDGE,"E61.MirrorC")}),-1.0]])]});
            extrude(context, id + "F15", {"entities" : qUnion([Q0, Q1, Q2, Q3, Q4, Q5, Q6, Q7, Q8, Q9, Q10, Q11, Q12, Q13, Q14]), "operationType" : NewBodyOperationType.REMOVE, "oppositeDirection" : true, "depth" : 97 * mm, "offsetDistance" : 25 * mm});
        }
        {
            var Q0;
            Q0=makeQuery(id+"F11.imprint","IMPRINT",FACE,{"disambiguationData":[TD([[makeQuery(id+"F11.imprint","IMPRINT",EDGE,{"derivedFrom":sQuery(id+"F11.wireOp",EDGE,"E123")}),1.0]])]});
            var Q1;
            Q1=makeQuery(id+"F11.imprint","IMPRINT",FACE,{"disambiguationData":[TD([[makeQuery(id+"F11.imprint","IMPRINT",EDGE,{"derivedFrom":sQuery(id+"F11.wireOp",EDGE,"E124")}),1.0]])]});
            var Q2;
            Q2=makeQuery(id+"F11.imprint","IMPRINT",FACE,{"disambiguationData":[TD([[makeQuery(id+"F11.imprint","IMPRINT",EDGE,{"derivedFrom":sQuery(id+"F11.wireOp",EDGE,"E130.MirrorC")}),-1.0]])]});
            var Q3;
            Q3=makeQuery(id+"F11.imprint","IMPRINT",FACE,{"disambiguationData":[TD([[makeQuery(id+"F11.imprint","IMPRINT",EDGE,{"derivedFrom":sQuery(id+"F11.wireOp",EDGE,"E131.MirrorC")}),-1.0]])]});
            var Q4;
            Q4=makeQuery(id+"F11.imprint","IMPRINT",FACE,{"disambiguationData":[TD([[makeQuery(id+"F11.imprint","IMPRINT",EDGE,{"derivedFrom":sQuery(id+"F11.wireOp",EDGE,"E126")}),1.0]])]});
            var Q5;
            Q5=makeQuery(id+"F11.imprint","IMPRINT",FACE,{"disambiguationData":[TD([[makeQuery(id+"F11.imprint","IMPRINT",EDGE,{"derivedFrom":sQuery(id+"F11.wireOp",EDGE,"E125")}),1.0]])]});
            var Q6;
            Q6=makeQuery(id+"F11.imprint","IMPRINT",FACE,{"disambiguationData":[TD([[makeQuery(id+"F11.imprint","IMPRINT",EDGE,{"derivedFrom":sQuery(id+"F11.wireOp",EDGE,"E122")}),1.0]])]});
            var Q7;
            Q7=makeQuery(id+"F11.imprint","IMPRINT",FACE,{"disambiguationData":[TD([[makeQuery(id+"F11.imprint","IMPRINT",EDGE,{"derivedFrom":sQuery(id+"F11.wireOp",EDGE,"E121")}),1.0]])]});
            var Q8;
            Q8=makeQuery(id+"F11.imprint","IMPRINT",FACE,{"disambiguationData":[TD([[makeQuery(id+"F11.imprint","IMPRINT",EDGE,{"derivedFrom":sQuery(id+"F11.wireOp",EDGE,"E119")}),1.0]])]});
            var Q9;
            Q9=makeQuery(id+"F11.imprint","IMPRINT",FACE,{"disambiguationData":[TD([[makeQuery(id+"F11.imprint","IMPRINT",EDGE,{"derivedFrom":sQuery(id+"F11.wireOp",EDGE,"E120")}),1.0]])]});
            var Q10;
            Q10=makeQuery(id+"F11.imprint","IMPRINT",FACE,{"disambiguationData":[TD([[makeQuery(id+"F11.imprint","IMPRINT",EDGE,{"derivedFrom":sQuery(id+"F11.wireOp",EDGE,"E118")}),1.0]])]});
            var Q11;
            Q11=makeQuery(id+"F11.imprint","IMPRINT",FACE,{"disambiguationData":[TD([[makeQuery(id+"F11.imprint","IMPRINT",EDGE,{"derivedFrom":sQuery(id+"F11.wireOp",EDGE,"E117")}),1.0]])]});
            var Q12;
            Q12=makeQuery(id+"F11.imprint","IMPRINT",FACE,{"disambiguationData":[TD([[makeQuery(id+"F11.imprint","IMPRINT",EDGE,{"derivedFrom":sQuery(id+"F11.wireOp",EDGE,"E116")}),1.0]])]});
            var Q13;
            Q13=makeQuery(id+"F11.imprint","IMPRINT",FACE,{"disambiguationData":[TD([[makeQuery(id+"F11.imprint","IMPRINT",EDGE,{"derivedFrom":sQuery(id+"F11.wireOp",EDGE,"E115")}),1.0]])]});
            var Q14;
            Q14=makeQuery(id+"F11.imprint","IMPRINT",FACE,{"disambiguationData":[TD([[makeQuery(id+"F11.imprint","IMPRINT",EDGE,{"derivedFrom":sQuery(id+"F11.wireOp",EDGE,"E114")}),1.0]])]});
            var Q15;
            Q15=makeQuery(id+"F11.imprint","IMPRINT",FACE,{"disambiguationData":[TD([[makeQuery(id+"F11.imprint","IMPRINT",EDGE,{"derivedFrom":sQuery(id+"F11.wireOp",EDGE,"E113")}),1.0]])]});
            var Q16;
            Q16=makeQuery(id+"F11.imprint","IMPRINT",FACE,{"disambiguationData":[TD([[makeQuery(id+"F11.imprint","IMPRINT",EDGE,{"derivedFrom":sQuery(id+"F11.wireOp",EDGE,"E110")}),1.0]])]});
            var Q17;
            Q17=makeQuery(id+"F11.imprint","IMPRINT",FACE,{"disambiguationData":[TD([[makeQuery(id+"F11.imprint","IMPRINT",EDGE,{"derivedFrom":sQuery(id+"F11.wireOp",EDGE,"E111")}),1.0]])]});
            var Q18;
            Q18=makeQuery(id+"F11.imprint","IMPRINT",FACE,{"disambiguationData":[TD([[makeQuery(id+"F11.imprint","IMPRINT",EDGE,{"derivedFrom":sQuery(id+"F11.wireOp",EDGE,"E112")}),1.0]])]});
            var Q19;
            Q19=makeQuery(id+"F11.imprint","IMPRINT",FACE,{"disambiguationData":[TD([[makeQuery(id+"F11.imprint","IMPRINT",EDGE,{"derivedFrom":sQuery(id+"F11.wireOp",EDGE,"E128")}),1.0]])]});
            var Q20;
            Q20=makeQuery(id+"F11.imprint","IMPRINT",FACE,{"disambiguationData":[TD([[makeQuery(id+"F11.imprint","IMPRINT",EDGE,{"derivedFrom":sQuery(id+"F11.wireOp",EDGE,"E147.MirrorC")}),-1.0]])]});
            var Q21;
            Q21=makeQuery(id+"F11.imprint","IMPRINT",FACE,{"disambiguationData":[TD([[makeQuery(id+"F11.imprint","IMPRINT",EDGE,{"derivedFrom":sQuery(id+"F11.wireOp",EDGE,"E146.MirrorC")}),-1.0]])]});
            var Q22;
            Q22=makeQuery(id+"F11.imprint","IMPRINT",FACE,{"disambiguationData":[TD([[makeQuery(id+"F11.imprint","IMPRINT",EDGE,{"derivedFrom":sQuery(id+"F11.wireOp",EDGE,"E145.MirrorC")}),-1.0]])]});
            var Q23;
            Q23=makeQuery(id+"F11.imprint","IMPRINT",FACE,{"disambiguationData":[TD([[makeQuery(id+"F11.imprint","IMPRINT",EDGE,{"derivedFrom":sQuery(id+"F11.wireOp",EDGE,"E144.MirrorC")}),-1.0]])]});
            var Q24;
            Q24=makeQuery(id+"F11.imprint","IMPRINT",FACE,{"disambiguationData":[TD([[makeQuery(id+"F11.imprint","IMPRINT",EDGE,{"derivedFrom":sQuery(id+"F11.wireOp",EDGE,"E143.MirrorC")}),-1.0]])]});
            var Q25;
            Q25=makeQuery(id+"F11.imprint","IMPRINT",FACE,{"disambiguationData":[TD([[makeQuery(id+"F11.imprint","IMPRINT",EDGE,{"derivedFrom":sQuery(id+"F11.wireOp",EDGE,"E142.MirrorC")}),-1.0]])]});
            var Q26;
            Q26=makeQuery(id+"F11.imprint","IMPRINT",FACE,{"disambiguationData":[TD([[makeQuery(id+"F11.imprint","IMPRINT",EDGE,{"derivedFrom":sQuery(id+"F11.wireOp",EDGE,"E141.MirrorC")}),-1.0]])]});
            var Q27;
            Q27=makeQuery(id+"F11.imprint","IMPRINT",FACE,{"disambiguationData":[TD([[makeQuery(id+"F11.imprint","IMPRINT",EDGE,{"derivedFrom":sQuery(id+"F11.wireOp",EDGE,"E127")}),1.0]])]});
            var Q28;
            Q28=makeQuery(id+"F11.imprint","IMPRINT",FACE,{"disambiguationData":[TD([[makeQuery(id+"F11.imprint","IMPRINT",EDGE,{"derivedFrom":sQuery(id+"F11.wireOp",EDGE,"E140.MirrorC")}),-1.0]])]});
            var Q29;
            Q29=makeQuery(id+"F11.imprint","IMPRINT",FACE,{"disambiguationData":[TD([[makeQuery(id+"F11.imprint","IMPRINT",EDGE,{"derivedFrom":sQuery(id+"F11.wireOp",EDGE,"E139.MirrorC")}),-1.0]])]});
            var Q30;
            Q30=makeQuery(id+"F11.imprint","IMPRINT",FACE,{"disambiguationData":[TD([[makeQuery(id+"F11.imprint","IMPRINT",EDGE,{"derivedFrom":sQuery(id+"F11.wireOp",EDGE,"E138.MirrorC")}),-1.0]])]});
            var Q31;
            Q31=makeQuery(id+"F11.imprint","IMPRINT",FACE,{"disambiguationData":[TD([[makeQuery(id+"F11.imprint","IMPRINT",EDGE,{"derivedFrom":sQuery(id+"F11.wireOp",EDGE,"E137.MirrorC")}),-1.0]])]});
            var Q32;
            Q32=makeQuery(id+"F11.imprint","IMPRINT",FACE,{"disambiguationData":[TD([[makeQuery(id+"F11.imprint","IMPRINT",EDGE,{"derivedFrom":sQuery(id+"F11.wireOp",EDGE,"E136.MirrorC")}),-1.0]])]});
            var Q33;
            Q33=makeQuery(id+"F11.imprint","IMPRINT",FACE,{"disambiguationData":[TD([[makeQuery(id+"F11.imprint","IMPRINT",EDGE,{"derivedFrom":sQuery(id+"F11.wireOp",EDGE,"E135.MirrorC")}),-1.0]])]});
            var Q34;
            Q34=makeQuery(id+"F11.imprint","IMPRINT",FACE,{"disambiguationData":[TD([[makeQuery(id+"F11.imprint","IMPRINT",EDGE,{"derivedFrom":sQuery(id+"F11.wireOp",EDGE,"E134.MirrorC")}),-1.0]])]});
            var Q35;
            Q35=makeQuery(id+"F11.imprint","IMPRINT",FACE,{"disambiguationData":[TD([[makeQuery(id+"F11.imprint","IMPRINT",EDGE,{"derivedFrom":sQuery(id+"F11.wireOp",EDGE,"E133.MirrorC")}),-1.0]])]});
            var Q36;
            Q36=makeQuery(id+"F11.imprint","IMPRINT",FACE,{"disambiguationData":[TD([[makeQuery(id+"F11.imprint","IMPRINT",EDGE,{"derivedFrom":sQuery(id+"F11.wireOp",EDGE,"E132.MirrorC")}),-1.0]])]});
            var Q37;
            Q37=makeQuery(id+"F11.imprint","IMPRINT",FACE,{"disambiguationData":[TD([[makeQuery(id+"F11.imprint","IMPRINT",EDGE,{"derivedFrom":sQuery(id+"F11.wireOp",EDGE,"E132.MirrorC")}),-1.0]])]});
            var Q38;
            Q38=makeQuery(id+"F11.imprint","IMPRINT",FACE,{"disambiguationData":[TD([[makeQuery(id+"F11.imprint","IMPRINT",EDGE,{"derivedFrom":sQuery(id+"F11.wireOp",EDGE,"E148.MirrorC")}),-1.0]])]});
            extrude(context, id + "F16", {"entities" : qUnion([Q0, Q1, Q2, Q3, Q4, Q5, Q6, Q7, Q8, Q9, Q10, Q11, Q12, Q13, Q14, Q15, Q16, Q17, Q18, Q19, Q20, Q21, Q22, Q23, Q24, Q25, Q26, Q27, Q28, Q29, Q30, Q31, Q32, Q33, Q34, Q35, Q36, Q37, Q38]), "operationType" : NewBodyOperationType.REMOVE, "oppositeDirection" : true, "depth" : 100 * mm, "offsetDistance" : 25 * mm});
        }
    });
